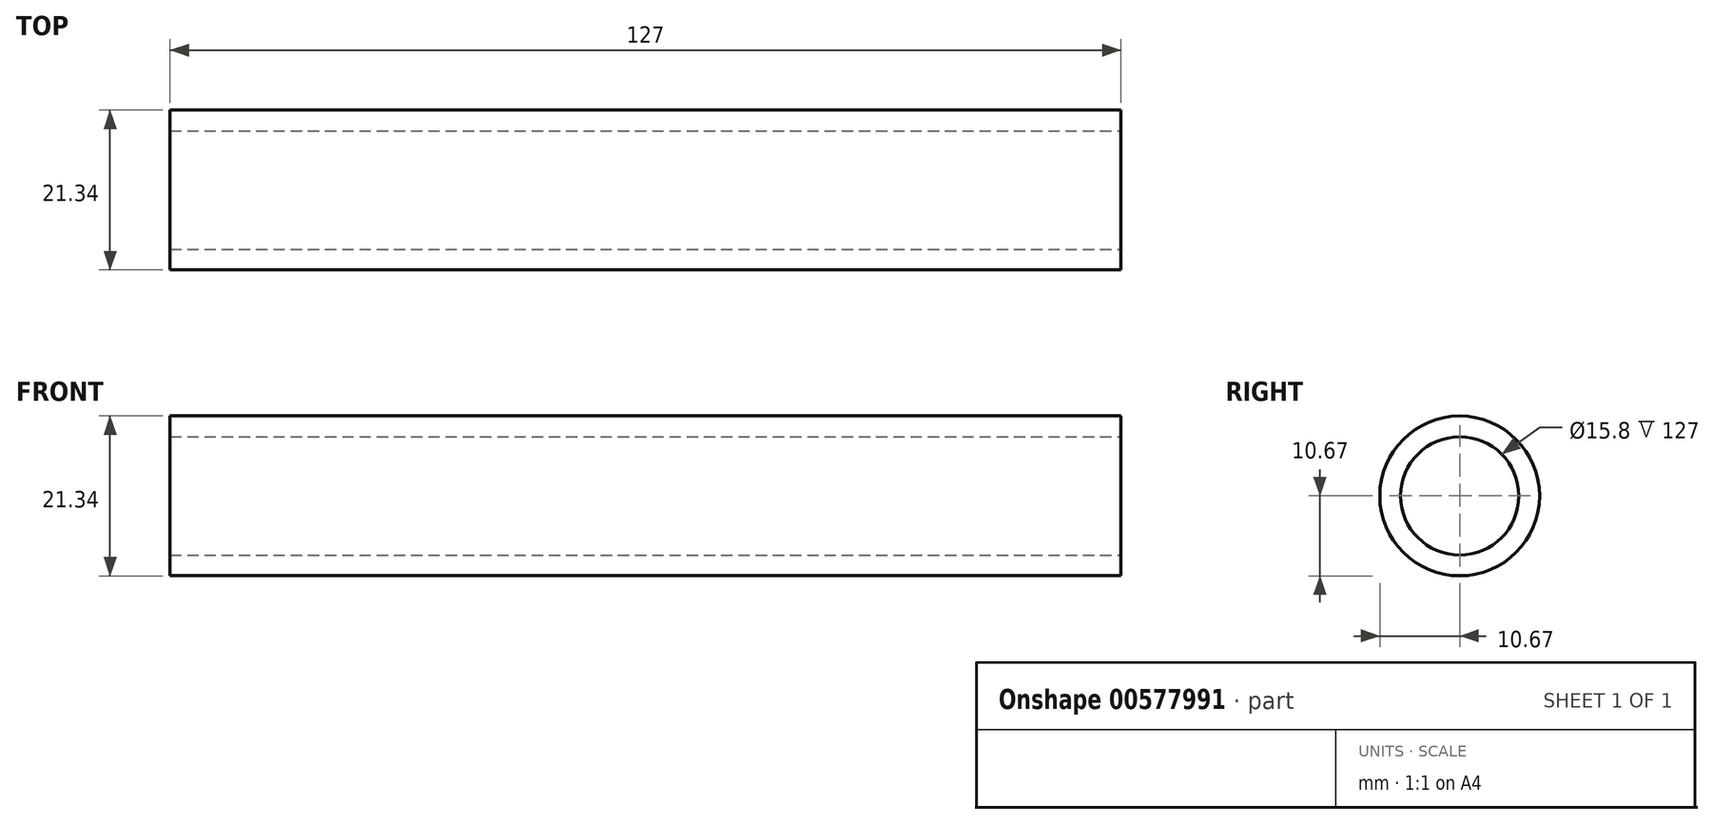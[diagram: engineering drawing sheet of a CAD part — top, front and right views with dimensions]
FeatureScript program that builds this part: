
annotation { "Feature Type Name" : "Feature", "Feature Type Description" : "" }
export const myFeature = defineFeature(function(context is Context, id is Id, definition is map)
    precondition{}
    {
        {
            var Q0;
            Q0=qCreatedBy(makeId("Right.planeOp"),FACE);
            var sketch = newSketch(context, id + "F0", { "sketchPlane" : qUnion([Q0])});
            skCircle(sketch, "E0", {"center": v(0, 0) * mm, "radius": 10.67 * mm});
            skSolve(sketch);
        }
        {
            var Q0;
            Q0=makeQuery(id+"F0.imprint","IMPRINT",FACE,{"disambiguationData":[TD([[makeQuery(id+"F0.imprint","IMPRINT",EDGE,{"derivedFrom":sQuery(id+"F0.wireOp",EDGE,"E0")}),1.0]])]});
            extrude(context, id + "F1", {"entities" : qUnion([Q0]), "flatOperationType" : FlatOperationType.REMOVE, "endBound" : BoundingType.SYMMETRIC, "offsetDistance" : 25.4 * mm, "depth" : 127 * mm, "domain" : OperationDomain.MODEL});
        }
        {
            var Q0;
            Q0=makeQuery(id+"F1.opExtrude","CAP_FACE",FACE,{"disambiguationData":[OSD([sQuery(id+"F0.wireOp",EDGE,"E0")])],"isStart":false});
            var sketch = newSketch(context, id + "F2", { "sketchPlane" : qUnion([Q0])});
            skCircle(sketch, "E1", {"center": v(0, 0) * mm, "radius": 7.9 * mm});
            skSolve(sketch);
        }
        {
            var Q0;
            Q0=sQuery(id+"F2.wireOp",VERTEX,"E1.center");
            var Q1;
            Q1=makeQuery(id+"F1.opExtrude","SWEPT_BODY",BODY,{"disambiguationData":[OSD([sQuery(id+"F0.wireOp",EDGE,"E0")])]});
            hole(context, id + "F3", {"style" : HoleStyle.SIMPLE, "endStyle" : HoleEndStyle.THROUGH, "holeDiameter" : 15.8 * mm, "tappedDepth" : 12.7 * mm, "tapClearance" : 3, "locations" : qUnion([Q0]), "scope" : qUnion([Q1])});
        }
    });
